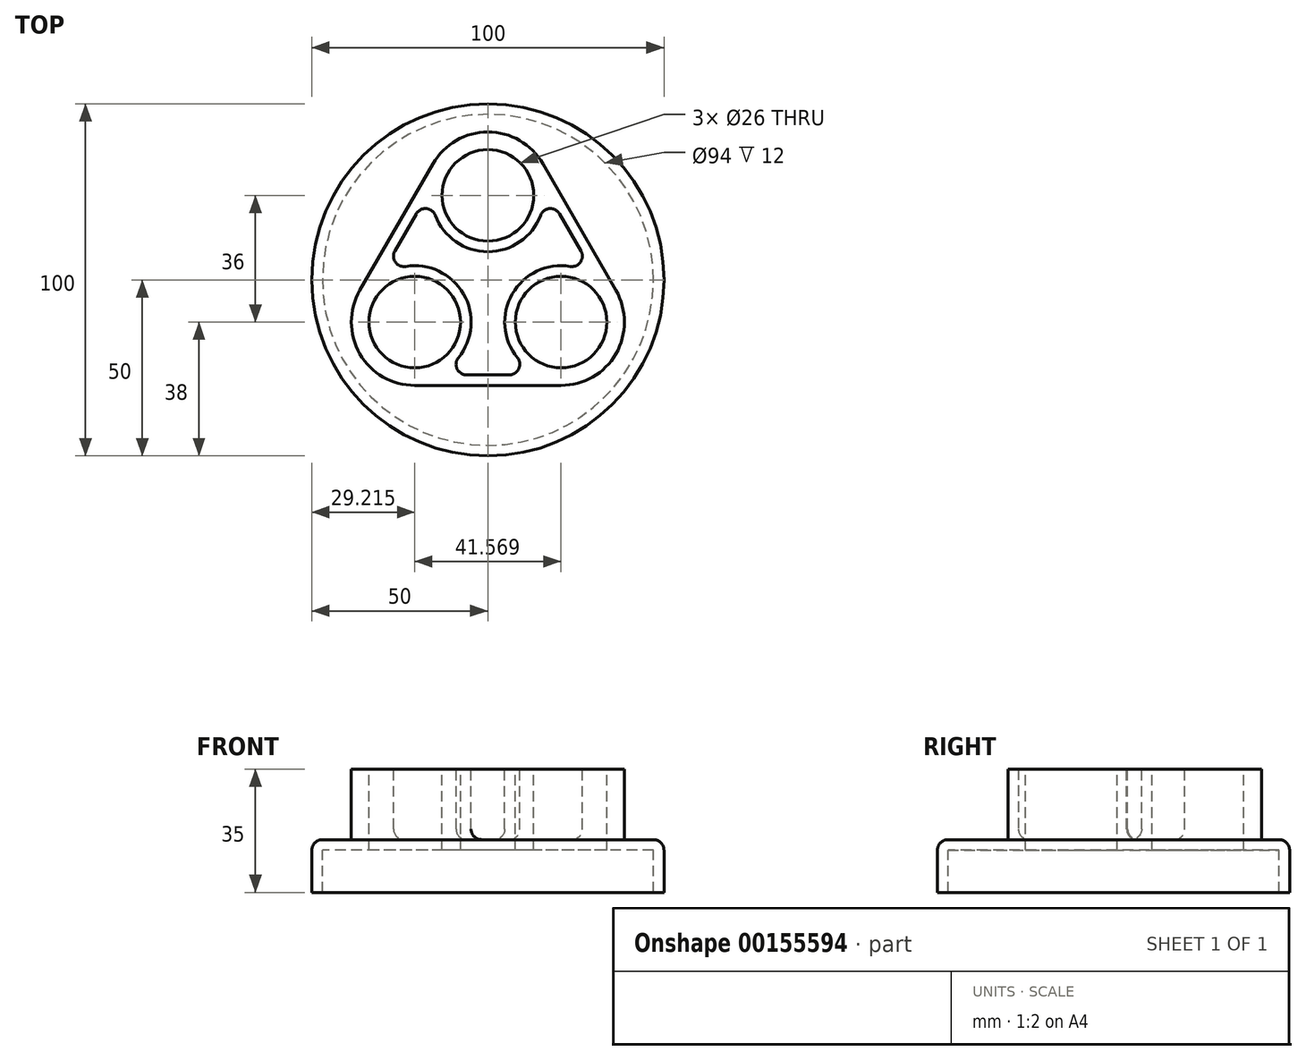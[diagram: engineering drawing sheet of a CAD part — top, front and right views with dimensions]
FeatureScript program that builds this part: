
annotation { "Feature Type Name" : "Feature", "Feature Type Description" : "" }
export const myFeature = defineFeature(function(context is Context, id is Id, definition is map)
    precondition{}
    {
        {
            var Q0;
            Q0=qCreatedBy(makeId("Top.planeOp"),FACE);
            var sketch = newSketch(context, id + "F0", { "sketchPlane" : qUnion([Q0])});
            skCircle(sketch, "E0", {"center": v(0, 0) * mm, "radius": 50 * mm});
            skSolve(sketch);
        }
        {
            var Q0;
            Q0 = qSketchRegion(id + "F0", true);
            extrude(context, id + "F1", {"entities" : qUnion([Q0]), "oppositeDirection" : true, "depth" : 15 * mm});
        }
        {
            var Q0;
            Q0=makeQuery(id+"F1.opExtrude","CAP_FACE",FACE,{"disambiguationData":[OSD([sQuery(id+"F0.wireOp",EDGE,"E0")])],"isStart":false});
            shell(context, id + "F2", {"entities" : qUnion([Q0]), "thickness" : 3 * mm});
        }
        {
            var Q0;
            Q0=makeQuery(id+"F1.opExtrude","CAP_FACE",FACE,{"disambiguationData":[OSD([sQuery(id+"F0.wireOp",EDGE,"E0")])],"isStart":true});
            var sketch = newSketch(context, id + "F3", { "sketchPlane" : qUnion([Q0])});
            skArc(sketch, "E1", {"start": v(15.59, 33) * mm, "mid": v(0, 42) * mm, "end": v(-15.59, 33) * mm});
            skArc(sketch, "E2.1.0", {"start": v(-36.37, -3) * mm, "mid": v(-36.37, -21) * mm, "end": v(-20.78, -30) * mm});
            skArc(sketch, "E2.2.0", {"start": v(20.78, -30) * mm, "mid": v(36.37, -21) * mm, "end": v(36.37, -3) * mm});
            skPoint(sketch, "E2.center", {"position": v(0, 0) * mm});
            skCircle(sketch, "E3", {"center": v(0, 0) * mm, "radius": 24 * mm, "construction": true});
            skLineSegment(sketch, "E4", {"start": v(15.59, 33) * mm, "end": v(36.37, -3) * mm});
            skLineSegment(sketch, "E5", {"start": v(-20.78, -30) * mm, "end": v(20.78, -30) * mm});
            skLineSegment(sketch, "E6", {"start": v(-15.59, 33) * mm, "end": v(-36.37, -3) * mm});
            skSolve(sketch);
        }
        {
            var Q0;
            Q0 = qSketchRegion(id + "F3", true);
            extrude(context, id + "F4", {"entities" : qUnion([Q0]), "operationType" : NewBodyOperationType.ADD, "depth" : (35 - 15) * mm});
        }
        {
            var Q0;
            Q0=makeQuery(id+"F4.opExtrude","CAP_FACE",FACE,{"disambiguationData":[OSD([sQuery(id+"F3.wireOp",EDGE,"E1"),sQuery(id+"F3.wireOp",EDGE,"E2.1.0"),sQuery(id+"F3.wireOp",EDGE,"E2.2.0"),sQuery(id+"F3.wireOp",EDGE,"E4"),sQuery(id+"F3.wireOp",EDGE,"E5"),sQuery(id+"F3.wireOp",EDGE,"E6")])],"isStart":false});
            var sketch = newSketch(context, id + "F5", { "sketchPlane" : qUnion([Q0])});
            skCircle(sketch, "E7", {"center": v(0, 24) * mm, "radius": 13 * mm});
            skCircle(sketch, "E8.1.0", {"center": v(-20.78, -12) * mm, "radius": 13 * mm});
            skCircle(sketch, "E8.2.0", {"center": v(20.78, -12) * mm, "radius": 13 * mm});
            skPoint(sketch, "E8.center", {"position": v(0, 0) * mm});
            skSolve(sketch);
        }
        {
            var Q0;
            Q0 = qSketchRegion(id + "F5", true);
            extrude(context, id + "F6", {"entities" : qUnion([Q0]), "operationType" : NewBodyOperationType.REMOVE, "endBound" : BoundingType.THROUGH_ALL, "oppositeDirection" : true, "depth" : 25 * mm});
        }
        {
            var Q0;
            Q0=makeQuery(id+"F4.opExtrude","CAP_FACE",FACE,{"disambiguationData":[OSD([sQuery(id+"F3.wireOp",EDGE,"E1"),sQuery(id+"F3.wireOp",EDGE,"E2.1.0"),sQuery(id+"F3.wireOp",EDGE,"E2.2.0"),sQuery(id+"F3.wireOp",EDGE,"E4"),sQuery(id+"F3.wireOp",EDGE,"E5"),sQuery(id+"F3.wireOp",EDGE,"E6")])],"isStart":false});
            shell(context, id + "F7", {"entities" : qUnion([Q0]), "thickness" : 3 * mm});
        }
        {
            var Q0;
            Q0=makeQuery(id+"F7.opShell","OFFSET_FACE",FACE,{"disambiguationData":[OSD([sQuery(id+"F0.wireOp",EDGE,"E0")])]});
            var Q1;
            Q1=makeQuery(id+"F7.opShell","TWEAK_EDGE",EDGE,{"derivedFrom":[makeQuery(id+"F4.opExtrude","SWEPT_FACE",FACE,{"disambiguationData":[OSD([sQuery(id+"F3.wireOp",EDGE,"E4")])]}),makeQuery(id+"F6.boolean.opBoolean","COPY",FACE,{"derivedFrom":makeQuery(id+"F6.opExtrude","SWEPT_FACE",FACE,{"disambiguationData":[OSD([sQuery(id+"F5.wireOp",EDGE,"E8.2.0")])]})})]});
            var Q2;
            Q2=makeQuery(id+"F7.opShell","TWEAK_EDGE",EDGE,{"derivedFrom":[makeQuery(id+"F4.opExtrude","SWEPT_FACE",FACE,{"disambiguationData":[OSD([sQuery(id+"F3.wireOp",EDGE,"E4")])]}),makeQuery(id+"F6.boolean.opBoolean","COPY",FACE,{"derivedFrom":makeQuery(id+"F6.opExtrude","SWEPT_FACE",FACE,{"disambiguationData":[OSD([sQuery(id+"F5.wireOp",EDGE,"E7")])]})})]});
            var Q3;
            Q3=makeQuery(id+"F7.opShell","TWEAK_EDGE",EDGE,{"derivedFrom":[makeQuery(id+"F4.opExtrude","SWEPT_FACE",FACE,{"disambiguationData":[OSD([sQuery(id+"F3.wireOp",EDGE,"E5")])]}),makeQuery(id+"F6.boolean.opBoolean","COPY",FACE,{"derivedFrom":makeQuery(id+"F6.opExtrude","SWEPT_FACE",FACE,{"disambiguationData":[OSD([sQuery(id+"F5.wireOp",EDGE,"E8.2.0")])]})})]});
            var Q4;
            Q4=makeQuery(id+"F7.opShell","TWEAK_EDGE",EDGE,{"derivedFrom":[makeQuery(id+"F4.opExtrude","SWEPT_FACE",FACE,{"disambiguationData":[OSD([sQuery(id+"F3.wireOp",EDGE,"E5")])]}),makeQuery(id+"F6.boolean.opBoolean","COPY",FACE,{"derivedFrom":makeQuery(id+"F6.opExtrude","SWEPT_FACE",FACE,{"disambiguationData":[OSD([sQuery(id+"F5.wireOp",EDGE,"E8.1.0")])]})})]});
            var Q5;
            Q5=makeQuery(id+"F7.opShell","TWEAK_EDGE",EDGE,{"derivedFrom":[makeQuery(id+"F4.opExtrude","SWEPT_FACE",FACE,{"disambiguationData":[OSD([sQuery(id+"F3.wireOp",EDGE,"E6")])]}),makeQuery(id+"F6.boolean.opBoolean","COPY",FACE,{"derivedFrom":makeQuery(id+"F6.opExtrude","SWEPT_FACE",FACE,{"disambiguationData":[OSD([sQuery(id+"F5.wireOp",EDGE,"E8.1.0")])]})})]});
            var Q6;
            Q6=makeQuery(id+"F7.opShell","TWEAK_EDGE",EDGE,{"derivedFrom":[makeQuery(id+"F4.opExtrude","SWEPT_FACE",FACE,{"disambiguationData":[OSD([sQuery(id+"F3.wireOp",EDGE,"E6")])]}),makeQuery(id+"F6.boolean.opBoolean","COPY",FACE,{"derivedFrom":makeQuery(id+"F6.opExtrude","SWEPT_FACE",FACE,{"disambiguationData":[OSD([sQuery(id+"F5.wireOp",EDGE,"E7")])]})})]});
            var Q7;
            Q7=makeQuery(id+"F4.opExtrude","CAP_EDGE",EDGE,{"disambiguationData":[OSD([sQuery(id+"F3.wireOp",EDGE,"E6")])],"isStart":true});
            var Q8;
            Q8=makeQuery(id+"F1.opExtrude","CAP_EDGE",EDGE,{"disambiguationData":[OSD([sQuery(id+"F0.wireOp",EDGE,"E0")])],"isStart":true});
            fillet(context, id + "F8", {"entities" : qUnion([Q0, Q1, Q2, Q3, Q4, Q5, Q6, Q7, Q8]), "radius" : 3 * mm, "tangentPropagation" : true, "allowEdgeOverflow" : false});
        }
    });
